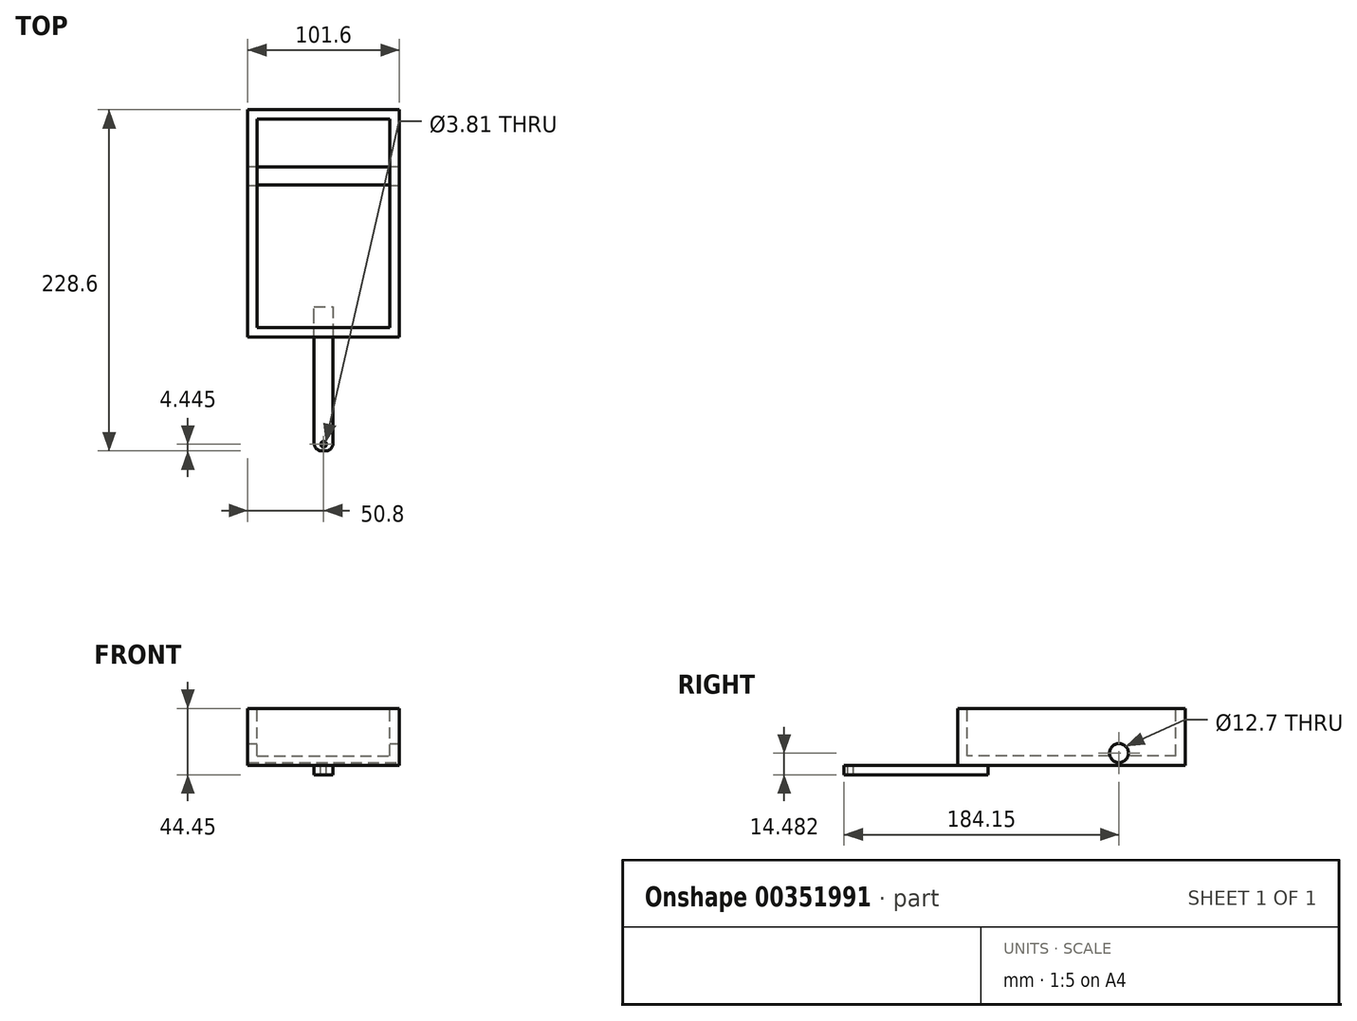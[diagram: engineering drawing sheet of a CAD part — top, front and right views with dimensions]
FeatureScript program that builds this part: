
annotation { "Feature Type Name" : "Feature", "Feature Type Description" : "" }
export const myFeature = defineFeature(function(context is Context, id is Id, definition is map)
    precondition{}
    {
        {
            var Q0;
            Q0=qCreatedBy(makeId("Right.planeOp"),FACE);
            var sketch = newSketch(context, id + "F0", { "sketchPlane" : qUnion([Q0])});
            skLineSegment(sketch, "E0.bottom", {"start": v(-76.2, 21.72) * mm, "end": v(76.2, 21.72) * mm});
            skLineSegment(sketch, "E0.top", {"start": v(-76.2, -16.38) * mm, "end": v(76.2, -16.38) * mm});
            skLineSegment(sketch, "E0.left", {"start": v(-76.2, 21.72) * mm, "end": v(-76.2, -16.38) * mm});
            skLineSegment(sketch, "E0.right", {"start": v(76.2, 21.72) * mm, "end": v(76.2, -16.38) * mm});
            skSolve(sketch);
        }
        {
            var Q0;
            Q0=makeQuery(id+"F0.imprint","IMPRINT",FACE,{"disambiguationData":[TD([[makeQuery(id+"F0.imprint","IMPRINT",EDGE,{"derivedFrom":sQuery(id+"F0.wireOp",EDGE,"E0.bottom")}),-1.0]])]});
            extrude(context, id + "F1", {"entities" : qUnion([Q0]), "depth" : 101.6 * mm});
        }
        {
            var Q0;
            Q0=makeQuery(id+"F1.opExtrude","SWEPT_FACE",FACE,{"disambiguationData":[OSD([sQuery(id+"F0.wireOp",EDGE,"E0.bottom")])]});
            var sketch = newSketch(context, id + "F2", { "sketchPlane" : qUnion([Q0])});
            skLineSegment(sketch, "E1.bottom", {"start": v(6.35, 69.85) * mm, "end": v(95.25, 69.85) * mm});
            skLineSegment(sketch, "E1.top", {"start": v(6.35, -69.85) * mm, "end": v(95.25, -69.85) * mm});
            skLineSegment(sketch, "E1.left", {"start": v(6.35, 69.85) * mm, "end": v(6.35, -69.85) * mm});
            skLineSegment(sketch, "E1.right", {"start": v(95.25, 69.85) * mm, "end": v(95.25, -69.85) * mm});
            skSolve(sketch);
        }
        {
            var Q0;
            Q0=makeQuery(id+"F2.imprint","IMPRINT",FACE,{"disambiguationData":[TD([[makeQuery(id+"F2.imprint","IMPRINT",EDGE,{"derivedFrom":sQuery(id+"F2.wireOp",EDGE,"E1.bottom")}),-1.0]])]});
            extrude(context, id + "F3", {"entities" : qUnion([Q0]), "operationType" : NewBodyOperationType.REMOVE, "oppositeDirection" : true, "depth" : 31.75 * mm});
        }
        {
            var Q0;
            Q0=makeQuery(id+"F1.opExtrude","CAP_FACE",FACE,{"disambiguationData":[OSD([sQuery(id+"F0.wireOp",EDGE,"E0.bottom"),sQuery(id+"F0.wireOp",EDGE,"E0.top"),sQuery(id+"F0.wireOp",EDGE,"E0.left"),sQuery(id+"F0.wireOp",EDGE,"E0.right")])],"isStart":false});
            var sketch = newSketch(context, id + "F4", { "sketchPlane" : qUnion([Q0])});
            skCircle(sketch, "E2", {"center": v(31.75, -8.25) * mm, "radius": 6.35 * mm});
            skSolve(sketch);
        }
        {
            var Q0;
            Q0=makeQuery(id+"F4.imprint","IMPRINT",FACE,{"disambiguationData":[TD([[makeQuery(id+"F4.imprint","IMPRINT",EDGE,{"derivedFrom":sQuery(id+"F4.wireOp",EDGE,"oWqWMlIe-qqx1-HBkg-gTyi-qKWSoIPXBaI8")}),1.0]])]});
            var Q1;
            Q1=makeQuery(id+"F4.imprint","IMPRINT",FACE,{"disambiguationData":[TD([[makeQuery(id+"F4.imprint","IMPRINT",EDGE,{"derivedFrom":sQuery(id+"F4.wireOp",EDGE,"E2")}),1.0]])]});
            extrude(context, id + "F5", {"entities" : qUnion([Q0, Q1]), "operationType" : NewBodyOperationType.REMOVE, "oppositeDirection" : true, "depth" : 101.6 * mm});
        }
        {
            var Q0;
            Q0=makeQuery(id+"F1.opExtrude","SWEPT_FACE",FACE,{"disambiguationData":[OSD([sQuery(id+"F0.wireOp",EDGE,"E0.top")])]});
            var sketch = newSketch(context, id + "F6", { "sketchPlane" : qUnion([Q0])});
            skLineSegment(sketch, "E3", {"start": v(44.45, 76.2) * mm, "end": v(44.45, 55.88) * mm});
            skLineSegment(sketch, "E4", {"start": v(44.45, 55.88) * mm, "end": v(57.15, 55.88) * mm});
            skLineSegment(sketch, "E5", {"start": v(57.15, 55.88) * mm, "end": v(57.15, 76.2) * mm});
            skSolve(sketch);
        }
        {
            var Q0;
            {var subQ0=sQuery(id+"F6.wireOp",EDGE,"E3");Q0=makeQuery(id+"F6.imprint","IMPRINT",FACE,{"disambiguationData":[TD([[makeQuery(id+"F6.imprint","IMPRINT",EDGE,{"derivedFrom":subQ0}),1.0]])]});}
            extrude(context, id + "F7", {"entities" : qUnion([Q0]), "operationType" : NewBodyOperationType.ADD, "depth" : 6.35 * mm});
        }
        {
            var Q0;
            {var subQ0=sQuery(id+"F0.wireOp",EDGE,"E0.left");Q0=makeQuery(id+"F7.boolean.opBoolean","MERGE",FACE,{"derivedFrom":[makeQuery(id+"F1.opExtrude","SWEPT_FACE",FACE,{"disambiguationData":[OSD([subQ0])]}),makeQuery(id+"F7.opExtrude","SWEPT_FACE",FACE,{"disambiguationData":[OSD([sQuery(id+"F0.wireOp",EDGE,"E0.top"),subQ0])]})]});}
            var sketch = newSketch(context, id + "F8", { "sketchPlane" : qUnion([Q0])});
            skLineSegment(sketch, "E6", {"start": v(44.45, -16.38) * mm, "end": v(57.15, -16.38) * mm});
            skSolve(sketch);
        }
        {
            var Q0;
            Q0=makeQuery(id+"F8.imprint","IMPRINT",FACE,{"disambiguationData":[TD([[makeQuery(id+"F8.imprint","IMPRINT",EDGE,{"derivedFrom":sQuery(id+"F8.wireOp",EDGE,"E6")}),-1.0]])]});
            extrude(context, id + "F9", {"entities" : qUnion([Q0]), "operationType" : NewBodyOperationType.ADD, "depth" : 76.2 * mm});
        }
        {
            var Q0;
            Q0=makeQuery(id+"F9.opExtrude","SWEPT_FACE",FACE,{"disambiguationData":[OSD([sQuery(id+"F8.wireOp",EDGE,"E6")])]});
            var sketch = newSketch(context, id + "F10", { "sketchPlane" : qUnion([Q0])});
            skCircle(sketch, "E7", {"center": v(50.8, -147.95) * mm, "radius": 1.9 * mm});
            skPoint(sketch, "E7.centerSnap0", {"position": v(50.8, -152.4) * mm});
            skSolve(sketch);
        }
        {
            var Q0;
            Q0=makeQuery(id+"F10.imprint","IMPRINT",FACE,{"disambiguationData":[TD([[makeQuery(id+"F10.imprint","IMPRINT",EDGE,{"derivedFrom":sQuery(id+"F10.wireOp",EDGE,"E7")}),1.0]])]});
            extrude(context, id + "F11", {"entities" : qUnion([Q0]), "operationType" : NewBodyOperationType.REMOVE, "oppositeDirection" : true, "depth" : 6.35 * mm});
        }
        {
            var Q0;
            Q0=makeQuery(id+"F9.opExtrude","CAP_EDGE",EDGE,{"disambiguationData":[OSD([sQuery(id+"F0.wireOp",EDGE,"E0.top"),sQuery(id+"F0.wireOp",EDGE,"E0.left"),sQuery(id+"F6.wireOp",EDGE,"E3")])],"isStart":false});
            fillet(context, id + "F12", {"entities" : qUnion([Q0]), "radius" : 5.08 * mm, "tangentPropagation" : true, "allowEdgeOverflow" : false});
        }
        {
            var Q0;
            Q0=makeQuery(id+"F9.opExtrude","CAP_EDGE",EDGE,{"disambiguationData":[OSD([sQuery(id+"F0.wireOp",EDGE,"E0.top"),sQuery(id+"F0.wireOp",EDGE,"E0.left"),sQuery(id+"F6.wireOp",EDGE,"E5")])],"isStart":false});
            fillet(context, id + "F13", {"entities" : qUnion([Q0]), "radius" : 5.08 * mm, "tangentPropagation" : true, "allowEdgeOverflow" : false});
        }
    });
